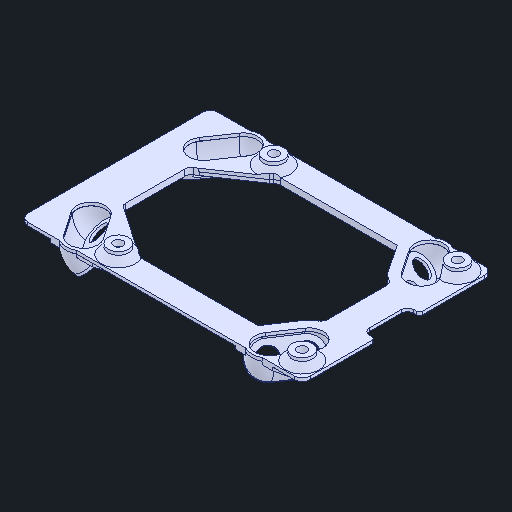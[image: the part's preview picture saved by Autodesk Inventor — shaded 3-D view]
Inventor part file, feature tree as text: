
AUTODESK INVENTOR PART (.ipt)
format: ipt  version: 2023 (Build 270158000, 158)  size: 567,296 bytes
history: native  units: in
note: dims shown in document units (in); Inventor stores cm internally (conversion verified against a paired STEP export)
features: other x1, fillet x1
ambient origin geometry x8: Origin, YZ Plane, XZ Plane, XY Plane, X Axis, Y Axis, Z Axis, Center Point
bodies: Solid1 (feature_tree)
feature tree (2):
  other  "VibroNavio2top_rev_A1"
  fillet  "Fillet4"  [1 undecoded]
note: 1 required parameter value undecoded (feature->parameter linkage not recoverable at this tier; creation-order binding heuristic only, values carry confidence <= 0.55)
